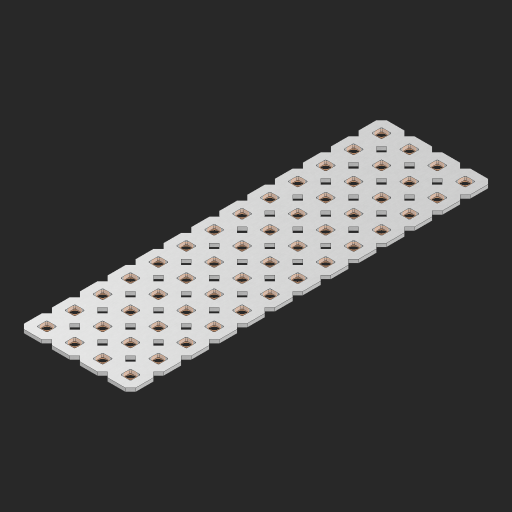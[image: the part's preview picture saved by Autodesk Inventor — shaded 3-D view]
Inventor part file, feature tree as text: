
AUTODESK INVENTOR PART (.ipt)
format: ipt  version: 2023 (Build 270158000, 158)  size: 887,296 bytes
history: native  units: in
note: dims shown in document units (in); Inventor stores cm internally (conversion verified against a paired STEP export)
features: other x53, extrude x51, sketch x2, pattern_linear x1
ambient origin geometry x8: Origin, YZ Plane, XZ Plane, XY Plane, X Axis, Y Axis, Z Axis, Center Point
bodies: Solid1 (feature_tree), Body (feature_tree)
feature tree (107):
  pattern_linear  "Rectangular Pattern1"  Spacing1=0.09in  [1 undecoded]
  sketch  "Sketch1"  dims[d1=0.5in]
  sketch  "Sketch2"  dims[d2=0.182in d3=0.09in d4=0.09in d5=0.09in d6=0.09in d7=0.09in d8=0.09in d9=0.09in d10=0.09in d11=0.02in d13=0.0in d14=0.172in d15=0.0625in d16=0.0in d19=0.5in d22=0.5in]
  other  "Srf1"
  other  "Srf126"
  other  "Srf127"
  other  "Srf128"
  other  "Srf129"
  other  "Srf130"
  other  "Srf131"
  other  "Srf250"
  other  "Srf251"
  other  "Srf252"
  other  "Srf253"
  other  "Srf254"
  other  "Srf255"
  other  "Srf268"
  other  "Srf269"
  other  "Srf270"
  other  "Srf271"
  other  "Srf272"
  other  "Srf273"
  other  "Srf274"
  other  "Srf275"
  other  "Srf276"
  other  "Srf277"
  other  "Srf278"
  other  "Srf279"
  other  "Srf280"
  other  "Srf293"
  other  "Srf294"
  other  "Srf295"
  other  "Srf296"
  other  "Srf297"
  other  "Srf298"
  other  "Srf299"
  other  "Srf300"
  other  "Srf301"
  other  "Srf302"
  other  "Srf303"
  other  "Srf304"
  other  "Srf305"
  other  "Srf318"
  other  "Srf319"
  other  "Srf320"
  other  "Srf321"
  other  "Srf322"
  other  "Srf323"
  other  "Srf324"
  other  "Srf325"
  other  "Srf326"
  other  "Srf327"
  other  "Srf328"
  other  "Srf329"
  other  "Srf330"
  other  "Circle"
  extrude  "ExtrusionSrf126"  Depth=0.09in
  extrude  "ExtrusionSrf127"  Depth=0.09in
  extrude  "ExtrusionSrf128"  Depth=0.09in
  extrude  "ExtrusionSrf129"  Depth=0.09in
  extrude  "ExtrusionSrf130"  Depth=0.09in
  extrude  "ExtrusionSrf131"  Depth=0.09in
  extrude  "ExtrusionSrf250"  Depth=0.09in
  extrude  "ExtrusionSrf251"  Depth=0.02in
  extrude  "ExtrusionSrf252"  TaperAngle=0.0deg  [1 undecoded]
  extrude  "ExtrusionSrf253"  Depth=0.5in
  extrude  "ExtrusionSrf254"  Depth=0.0625in TaperAngle=0.0deg
  extrude  "ExtrusionSrf255"  Depth=0.5in
  extrude  "ExtrusionSrf268"  Depth=0.5in
  extrude  "ExtrusionSrf269"  [1 undecoded]
  extrude  "ExtrusionSrf270"  [1 undecoded]
  extrude  "ExtrusionSrf271"  [1 undecoded]
  extrude  "ExtrusionSrf272"  [1 undecoded]
  extrude  "ExtrusionSrf273"  [1 undecoded]
  extrude  "ExtrusionSrf274"  [1 undecoded]
  extrude  "ExtrusionSrf275"  [1 undecoded]
  extrude  "ExtrusionSrf276"  [1 undecoded]
  extrude  "ExtrusionSrf277"  [1 undecoded]
  extrude  "ExtrusionSrf278"  [1 undecoded]
  extrude  "ExtrusionSrf279"  [1 undecoded]
  extrude  "ExtrusionSrf280"  [1 undecoded]
  extrude  "ExtrusionSrf293"  [1 undecoded]
  extrude  "ExtrusionSrf294"  [1 undecoded]
  extrude  "ExtrusionSrf295"  [1 undecoded]
  extrude  "ExtrusionSrf296"  [1 undecoded]
  extrude  "ExtrusionSrf297"  [1 undecoded]
  extrude  "ExtrusionSrf298"  [1 undecoded]
  extrude  "ExtrusionSrf299"  [1 undecoded]
  extrude  "ExtrusionSrf300"  [1 undecoded]
  extrude  "ExtrusionSrf301"  [1 undecoded]
  extrude  "ExtrusionSrf302"  [1 undecoded]
  extrude  "ExtrusionSrf303"  [1 undecoded]
  extrude  "ExtrusionSrf304"  [1 undecoded]
  extrude  "ExtrusionSrf305"  [1 undecoded]
  extrude  "ExtrusionSrf318"  [1 undecoded]
  extrude  "ExtrusionSrf319"  [1 undecoded]
  extrude  "ExtrusionSrf320"  [1 undecoded]
  extrude  "ExtrusionSrf321"  [1 undecoded]
  extrude  "ExtrusionSrf322"  [1 undecoded]
  extrude  "ExtrusionSrf323"  [1 undecoded]
  extrude  "ExtrusionSrf324"  [1 undecoded]
  extrude  "ExtrusionSrf325"  [1 undecoded]
  extrude  "ExtrusionSrf326"  [1 undecoded]
  extrude  "ExtrusionSrf327"  [1 undecoded]
  extrude  "ExtrusionSrf328"  [1 undecoded]
  extrude  "ExtrusionSrf329"  [1 undecoded]
  extrude  "ExtrusionSrf330"  [1 undecoded]
note: 40 required parameter values undecoded (feature->parameter linkage not recoverable at this tier; creation-order binding heuristic only, values carry confidence <= 0.55)
